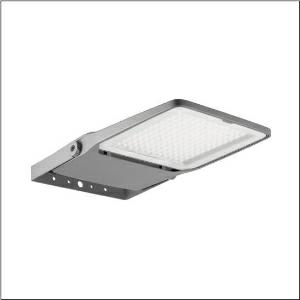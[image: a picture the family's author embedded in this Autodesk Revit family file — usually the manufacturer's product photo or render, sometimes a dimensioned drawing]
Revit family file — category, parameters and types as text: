
# Revit family: floodlight_fl_20_midi___pl43_5xa7682d3a2ac_b539
name_source: partatom
category: Lighting Fixtures
units: mm (PartAtom-declared; Revit-internal decimal feet)

## family parameters
Cut with Voids When Loaded = No
Host = Face
Light Source = No
Part Type = Normal
Room Calculation Point = No
Round Connector Dimension = Use Diameter
Shared = No

## types (1)
- --- (1 x LED 5000K / CRI = 70 (unbekannt), 19360 lm, 5000K)
    Apparent Load = 142 VA
    CIE Flux Codes = 32 74 99 100 100
    Color Rendering = 70
    Color Temperature = 5000K
    Default Elevation = 1800 mm
    Description = Floodlight FL 20 midi, floodlight, primary light control with lens, of plastic, primary optical cover: protective disc, of toughened safety glass, transparent, light distribution: PL43, light emission: direct distribution, primary light characteristic: asymmetric, installation type: surface-mounted, LED High Power LED, rated luminous flux: 19.360 lm, light colour: 750, colour temperature: 5000K, control gear: ECG Plus, control: flexible luminous flux parameterisation, time-dependent luminous flux control, digital communication interface, power reduction, overheat protection, electronic power reduction, with terminal, 5-pole, max. 2.5mm², mains connection: 220..240V, AC, 50/60Hz, rated input power: 142W, LED unit, of diecast aluminium, powder-coated, Siteco® metallic grey (DB 702S), length: 731 mm, width: 450 mm, height: 76mm, housing frame, of diecast aluminium, powder-coated, Siteco® metallic grey (DB 702S), wall fastening, of steel, powder-coated, Siteco® metallic grey (DB 702S), DALIprotection rating (complete): IP66, insulation class (complete): insulation class II (safety insulation), certification: CE, ENEC, VDE, protection symbol: D, permissible ambient temperature for indoor applications: -40..+40°C, permissible ambient temperature for outdoor applications: -40..+50°C, standard: DIN EN 12944, packaging unit: 1 piece

Light Distribution: PL43
    Height = 76 mm
    Lamp = 1 x LED 5000K / CRI >= 70 (unbekannt)
    Lamp Light Flux = 19360 lm
    Lamp count = 1
    Length = 731 mm
    Luminous efficacy = 136 lm/W
    Manufacturer = Siteco
    ModVariant = No
    Model = 5XA7682D3A2AC
    Number of Poles = 1
    OnlyDefault = Yes
    Power Factor = 1
    Product Name = Floodlight FL 20 midi | PL43
    Product group = floodlight | pylon top
    ProductGroupID = 6101
    Protection Class = Protection class II
    Protection Degree = IP 66
    RLX_Detail_Level = 1
    RlxData = <blob elided: 91677 chars, md5=fc3c21eb>
    Socket = socket
    Standby Power = 0 W
    System Light Flux = 19360 lm
    System Power = 142 W
    Type Comments = factory setting: luminous flux: 100 % | dim-lin: 254 | 489 mA
    Type Image = l_1005944.jpg
    URL = http://relux.com
    VarID = @adj_143875
    Voltage = 0 V
    Weight = 0.00 kg
    Width = 450 mm

## geometry (parser evidence)
native form markers: Blend x4, Sweep x13
no freeform markers — native parametric forms only
